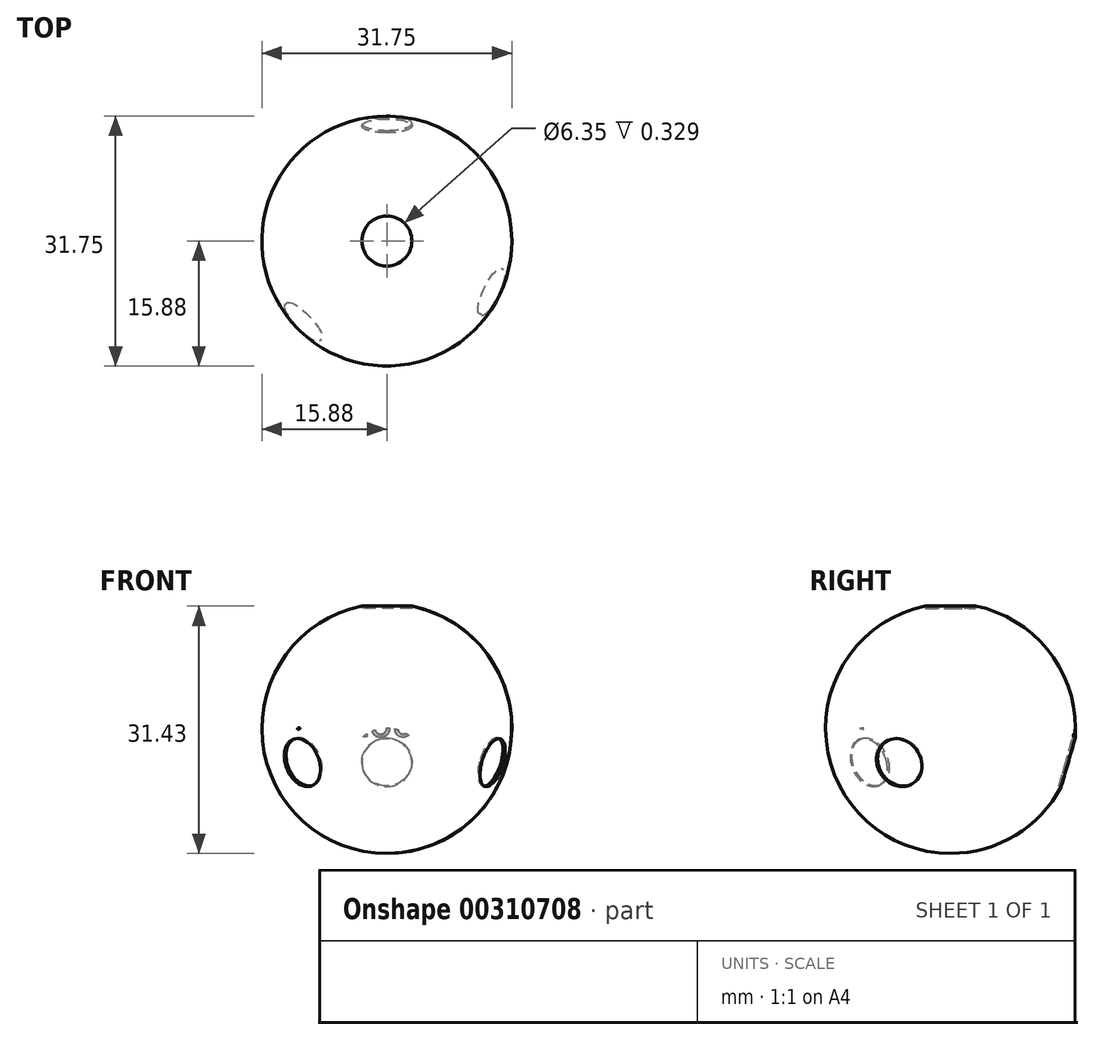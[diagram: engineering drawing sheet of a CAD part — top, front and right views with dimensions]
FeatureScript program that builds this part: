
annotation { "Feature Type Name" : "Feature", "Feature Type Description" : "" }
export const myFeature = defineFeature(function(context is Context, id is Id, definition is map)
    precondition{}
    {
        {
            var Q0;
            Q0=qCreatedBy(makeId("Front.planeOp"),FACE);
            var sketch = newSketch(context, id + "F0", { "sketchPlane" : qUnion([Q0])});
            skArc(sketch, "E0", {"start": v(0, 15.88) * mm, "mid": v(-15.88, 0) * mm, "end": v(0, -15.88) * mm});
            skLineSegment(sketch, "E1", {"start": v(0, 15.88) * mm, "end": v(0, -15.88) * mm});
            skSolve(sketch);
        }
        {
            var Q0;
            Q0=qCreatedBy(makeId("Top.planeOp"),FACE);
            var sketch = newSketch(context, id + "F1", { "sketchPlane" : qUnion([Q0])});
            skCircle(sketch, "E2", {"center": v(0, 0) * mm, "radius": 15.88 * mm});
            skSolve(sketch);
        }
        {
            var Q0;
            Q0=makeQuery(id+"F0.imprint","IMPRINT",FACE,{"disambiguationData":[TD([[makeQuery(id+"F0.imprint","IMPRINT",EDGE,{"derivedFrom":sQuery(id+"F0.wireOp",EDGE,"E0")}),1.0]])]});
            var Q1;
            Q1=sQuery(id+"F1.wireOp",EDGE,"E2");
            revolve(context, id + "F2", {"entities" : qUnion([Q0]), "axis" : qUnion([Q1]), "revolveType" : RevolveType.FULL});
        }
        {
            var Q0;
            Q0=qCreatedBy(makeId("Top.planeOp"),FACE);
            cPlane(context, id + "F3", {"entities" : qUnion([Q0]), "cplaneType" : CPlaneType.OFFSET, "offset" : 15.24 * mm, "width" : 152.4 * mm, "height" : 152.4 * mm});
        }
        {
            var Q0;
            Q0=qCreatedBy(id+"F3.planeOp",FACE);
            cPlane(context, id + "F4", {"entities" : qUnion([Q0]), "cplaneType" : CPlaneType.OFFSET, "offset" : 3 / 203.2 * mm, "oppositeDirection" : true, "width" : 152.4 * mm, "height" : 152.4 * mm});
        }
        {
            var Q0;
            Q0=qCreatedBy(id+"F4.planeOp",FACE);
            var sketch = newSketch(context, id + "F5", { "sketchPlane" : qUnion([Q0])});
            skCircle(sketch, "E3", {"center": v(0, 0) * mm, "radius": 3.18 * mm});
            skSolve(sketch);
        }
        {
            var Q0;
            Q0 = qSketchRegion(id + "F5", true);
            extrude(context, id + "F6", {"entities" : qUnion([Q0]), "depth" : 50.8 * mm});
        }
        {
            var Q0;
            Q0=qCreatedBy(makeId("Front.planeOp"),FACE);
            var sketch = newSketch(context, id + "F7", { "sketchPlane" : qUnion([Q0])});
            skLineSegment(sketch, "E4", {"start": v(0, 0) * mm, "end": v(0, -53.82) * mm, "construction": true});
            skLineSegment(sketch, "E5", {"start": v(0, 0) * mm, "end": v(-63.8, 0) * mm, "construction": true});
            skSolve(sketch);
        }
        {
            var Q0;
            Q0=makeQuery(id+"F6.opExtrude","SWEPT_BODY",BODY,{"disambiguationData":[OSD([sQuery(id+"F5.wireOp",EDGE,"E3")])]});
            var Q1;
            Q1=sQuery(id+"F7.wireOp",EDGE,"E5");
            transform(context, id + "F8", {"entities" : qUnion([Q0]), "transformType" : TransformType.ROTATION, "transformAxis" : qUnion([Q1]), "angle" : 106.2 * degree, "makeCopy" : true});
        }
        {
            var Q0;
            Q0=makeQuery(id+"F8.opPattern","COPY",BODY,{"derivedFrom":makeQuery(id+"F6.opExtrude","SWEPT_BODY",BODY,{"disambiguationData":[OSD([sQuery(id+"F5.wireOp",EDGE,"E3")])]}),"instanceName":"1"});
            var Q1;
            Q1=sQuery(id+"F7.wireOp",EDGE,"E4");
            transform(context, id + "F9", {"entities" : qUnion([Q0]), "transformType" : TransformType.ROTATION, "transformAxis" : qUnion([Q1]), "angle" : 115.9 * degree, "makeCopy" : true});
        }
        {
            var Q0;
            Q0=makeQuery(id+"F9.opPattern","COPY",BODY,{"derivedFrom":makeQuery(id+"F8.opPattern","COPY",BODY,{"derivedFrom":makeQuery(id+"F6.opExtrude","SWEPT_BODY",BODY,{"disambiguationData":[OSD([sQuery(id+"F5.wireOp",EDGE,"E3")])]}),"instanceName":"1"}),"instanceName":"1"});
            var Q1;
            Q1=sQuery(id+"F7.wireOp",EDGE,"E4");
            var Q2;
            Q2=sQuery(id+"F7.wireOp",EDGE,"E4");
            transform(context, id + "F10", {"entities" : qUnion([Q0]), "transformType" : TransformType.ROTATION, "transformAxis" : qUnion([Q2]), "angle" : 110 * degree, "makeCopy" : true});
        }
        {
            var Q0;
            Q0=makeQuery(id+"F8.opPattern","COPY",FACE,{"derivedFrom":makeQuery(id+"F6.opExtrude","CAP_FACE",FACE,{"disambiguationData":[OSD([sQuery(id+"F5.wireOp",EDGE,"E3")])],"isStart":false}),"instanceName":"1"});
            cPlane(context, id + "F11", {"entities" : qUnion([Q0]), "cplaneType" : CPlaneType.OFFSET, "offset" : 25.4 * mm, "oppositeDirection" : true, "width" : 152.4 * mm, "height" : 152.4 * mm});
        }
        {
            var Q0;
            Q0=qCreatedBy(id+"F11.planeOp",FACE);
            var sketch = newSketch(context, id + "F12", { "sketchPlane" : qUnion([Q0])});
            skText(sketch, "E6", { "text": "106.2\n", "fontName": "OpenSans-Regular.ttf"});
            const initialGuessF12  = {"E6": [-0.0063, 0.00336, 1, 0, 0.00354]};
            skSetInitialGuess(sketch, initialGuessF12);
            skSolve(sketch);
        }
        {
            var Q0;
            Q0 = qSketchRegion(id + "F12", true);
            extrude(context, id + "F13", {"entities" : qUnion([Q0]), "operationType" : NewBodyOperationType.REMOVE, "oppositeDirection" : true, "depth" : 25.4 * mm});
        }
        {
            var Q0;
            Q0=makeQuery(id+"F10.opPattern","COPY",FACE,{"derivedFrom":makeQuery(id+"F9.opPattern","COPY",FACE,{"derivedFrom":makeQuery(id+"F8.opPattern","COPY",FACE,{"derivedFrom":makeQuery(id+"F6.opExtrude","CAP_FACE",FACE,{"disambiguationData":[OSD([sQuery(id+"F5.wireOp",EDGE,"E3")])],"isStart":false}),"instanceName":"1"}),"instanceName":"1"}),"instanceName":"1"});
            cPlane(context, id + "F14", {"entities" : qUnion([Q0]), "cplaneType" : CPlaneType.OFFSET, "offset" : 25.4 * mm, "oppositeDirection" : true, "width" : 152.4 * mm, "height" : 152.4 * mm});
        }
        {
            var Q0;
            Q0=qCreatedBy(id+"F14.planeOp",FACE);
            var sketch = newSketch(context, id + "F15", { "sketchPlane" : qUnion([Q0])});
            skText(sketch, "E7", { "text": "110", "fontName": "OpenSans-Regular.ttf"});
            const initialGuessF15  = {"E7": [-0.00485, 0.00413, 1, 0, 0.00521]};
            skSetInitialGuess(sketch, initialGuessF15);
            skSolve(sketch);
        }
        {
            var Q0;
            Q0 = qSketchRegion(id + "F15", true);
            extrude(context, id + "F16", {"entities" : qUnion([Q0]), "operationType" : NewBodyOperationType.REMOVE, "oppositeDirection" : true, "depth" : 25.4 * mm});
        }
        {
            var Q0;
            Q0=makeQuery(id+"F6.opExtrude","SWEPT_BODY",BODY,{"disambiguationData":[OSD([sQuery(id+"F5.wireOp",EDGE,"E3")])]});
            var Q1;
            Q1=makeQuery(id+"F8.opPattern","COPY",BODY,{"derivedFrom":makeQuery(id+"F6.opExtrude","SWEPT_BODY",BODY,{"disambiguationData":[OSD([sQuery(id+"F5.wireOp",EDGE,"E3")])]}),"instanceName":"1"});
            var Q2;
            Q2=makeQuery(id+"F10.opPattern","COPY",BODY,{"derivedFrom":makeQuery(id+"F9.opPattern","COPY",BODY,{"derivedFrom":makeQuery(id+"F8.opPattern","COPY",BODY,{"derivedFrom":makeQuery(id+"F6.opExtrude","SWEPT_BODY",BODY,{"disambiguationData":[OSD([sQuery(id+"F5.wireOp",EDGE,"E3")])]}),"instanceName":"1"}),"instanceName":"1"}),"instanceName":"1"});
            var Q3;
            Q3=makeQuery(id+"F9.opPattern","COPY",BODY,{"derivedFrom":makeQuery(id+"F8.opPattern","COPY",BODY,{"derivedFrom":makeQuery(id+"F6.opExtrude","SWEPT_BODY",BODY,{"disambiguationData":[OSD([sQuery(id+"F5.wireOp",EDGE,"E3")])]}),"instanceName":"1"}),"instanceName":"1"});
            var Q4;
            Q4=makeQuery(id+"F2.opRevolve","SWEPT_BODY",BODY,{"disambiguationData":[OSD([sQuery(id+"F0.wireOp",EDGE,"E0"),sQuery(id+"F0.wireOp",EDGE,"E1")])]});
            booleanBodies(context, id + "F17", {"operationType" : BooleanOperationType.SUBTRACTION, "tools" : qUnion([Q0, Q1, Q2, Q3]), "targets" : qUnion([Q4])});
        }
    });
